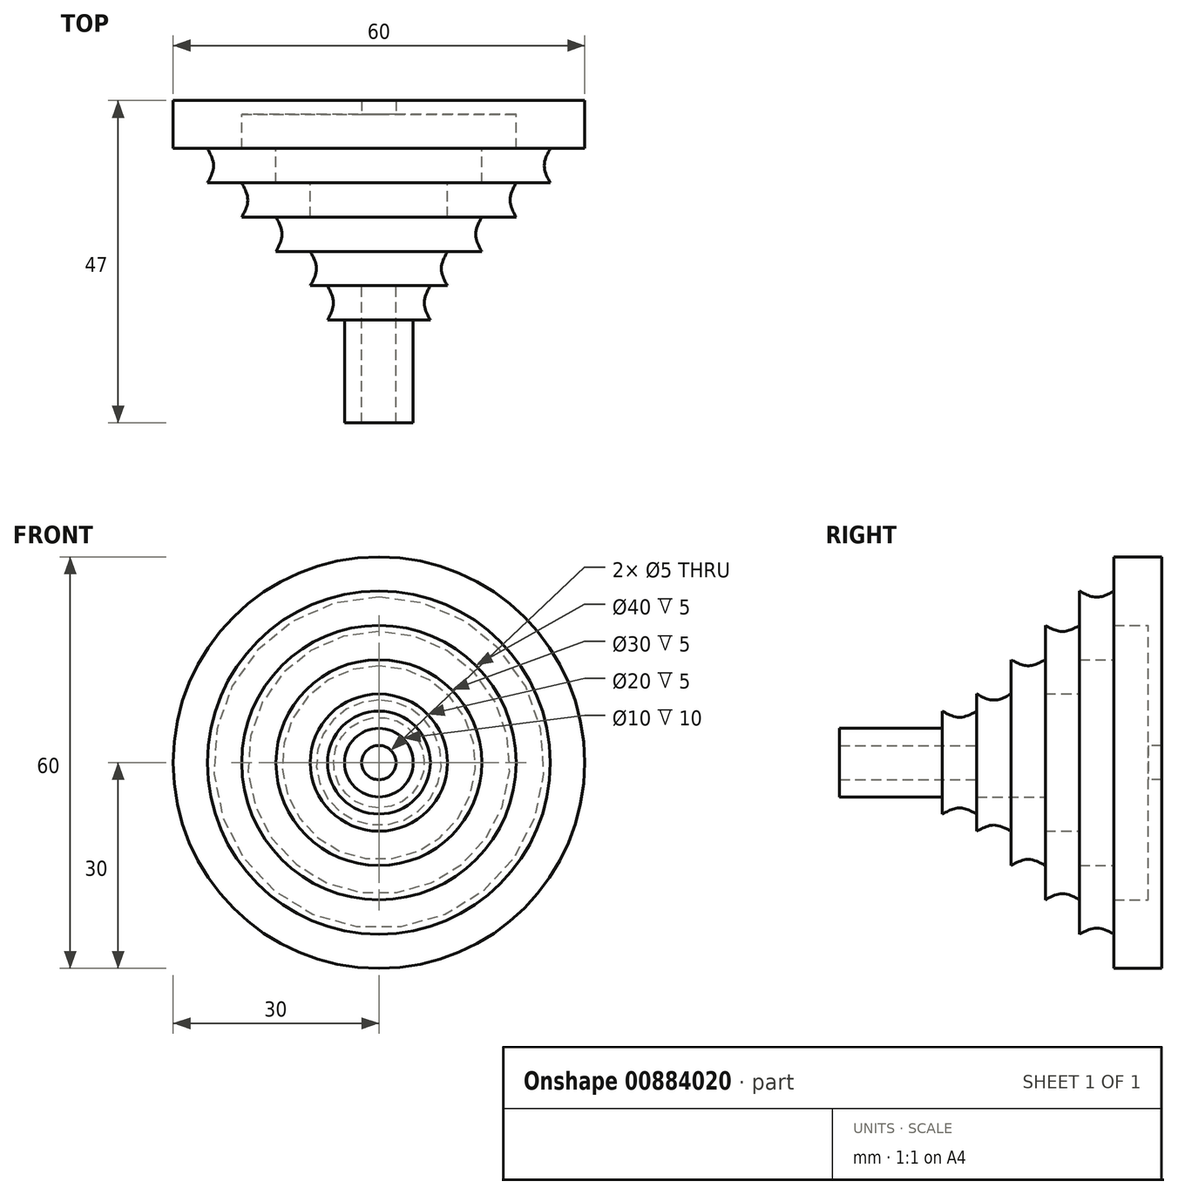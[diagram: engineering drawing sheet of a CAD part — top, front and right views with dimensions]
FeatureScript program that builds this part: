
annotation { "Feature Type Name" : "Feature", "Feature Type Description" : "" }
export const myFeature = defineFeature(function(context is Context, id is Id, definition is map)
    precondition{}
    {
        {
            var Q0;
            Q0=qCreatedBy(makeId("Front.planeOp"),FACE);
            var sketch = newSketch(context, id + "F0", { "sketchPlane" : qUnion([Q0])});
            skCircle(sketch, "E0", {"center": v(0, 0) * mm, "radius": 30 * mm});
            skCircle(sketch, "E1", {"center": v(0, 0) * mm, "radius": 20 * mm});
            skSolve(sketch);
        }
        {
            var Q0;
            Q0=makeQuery(id+"F0.imprint","IMPRINT",FACE,{"disambiguationData":[TD([[makeQuery(id+"F0.imprint","IMPRINT",EDGE,{"derivedFrom":sQuery(id+"F0.wireOp",EDGE,"E0")}),1.0]])]});
            extrude(context, id + "F1", {"entities" : qUnion([Q0]), "depth" : 5 * mm, "offsetDistance" : 25 * mm});
        }
        {
            var Q0;
            Q0=makeQuery(id+"F1.opExtrude","CAP_FACE",FACE,{"disambiguationData":[OSD([sQuery(id+"F0.wireOp",EDGE,"E0"),sQuery(id+"F0.wireOp",EDGE,"E1")])],"isStart":false});
            var sketch = newSketch(context, id + "F2", { "sketchPlane" : qUnion([Q0])});
            skCircle(sketch, "E2", {"center": v(0, 0) * mm, "radius": 25 * mm});
            skCircle(sketch, "E3", {"center": v(0, 0) * mm, "radius": 15 * mm});
            skSolve(sketch);
        }
        {
            var Q0;
            Q0=makeQuery(id+"F2.imprint","IMPRINT",FACE,{"disambiguationData":[TD([[makeQuery(id+"F2.imprint","IMPRINT",EDGE,{"derivedFrom":sQuery(id+"F2.wireOp",EDGE,"E3")}),-1.0]])]});
            var Q1;
            Q1=makeQuery(id+"F2.imprint","IMPRINT",FACE,{"disambiguationData":[TD([[makeQuery(id+"F2.imprint","IMPRINT",EDGE,{"derivedFrom":sQuery(id+"F2.wireOp",EDGE,"E2")}),1.0]])]});
            extrude(context, id + "F3", {"entities" : qUnion([Q0, Q1]), "operationType" : NewBodyOperationType.ADD, "depth" : 5 * mm, "offsetDistance" : 25 * mm});
        }
        {
            var Q0;
            Q0=makeQuery(id+"F3.opExtrude","CAP_FACE",FACE,{"disambiguationData":[OSD([sQuery(id+"F2.wireOp",EDGE,"E2"),sQuery(id+"F2.wireOp",EDGE,"E3")])],"isStart":false});
            var sketch = newSketch(context, id + "F4", { "sketchPlane" : qUnion([Q0])});
            skCircle(sketch, "E4", {"center": v(0, 0) * mm, "radius": 20 * mm});
            skCircle(sketch, "E5", {"center": v(0, 0) * mm, "radius": 10 * mm});
            skSolve(sketch);
        }
        {
            var Q0;
            Q0=makeQuery(id+"F4.imprint","IMPRINT",FACE,{"disambiguationData":[TD([[makeQuery(id+"F4.imprint","IMPRINT",EDGE,{"derivedFrom":sQuery(id+"F4.wireOp",EDGE,"E4")}),1.0]])]});
            var Q1;
            Q1=makeQuery(id+"F4.imprint","IMPRINT",FACE,{"disambiguationData":[TD([[makeQuery(id+"F4.imprint","IMPRINT",EDGE,{"derivedFrom":sQuery(id+"F4.wireOp",EDGE,"E5")}),-1.0]])]});
            extrude(context, id + "F5", {"entities" : qUnion([Q0, Q1]), "operationType" : NewBodyOperationType.ADD, "depth" : 5 * mm, "offsetDistance" : 25 * mm});
        }
        {
            var Q0;
            Q0=makeQuery(id+"F5.opExtrude","CAP_FACE",FACE,{"disambiguationData":[OSD([sQuery(id+"F4.wireOp",EDGE,"E4"),sQuery(id+"F4.wireOp",EDGE,"E5")])],"isStart":false});
            var sketch = newSketch(context, id + "F6", { "sketchPlane" : qUnion([Q0])});
            skCircle(sketch, "E6", {"center": v(0, 0) * mm, "radius": 15 * mm});
            skCircle(sketch, "E7", {"center": v(0, 0) * mm, "radius": 5 * mm});
            skSolve(sketch);
        }
        {
            var Q0;
            Q0=makeQuery(id+"F6.imprint","IMPRINT",FACE,{"disambiguationData":[TD([[makeQuery(id+"F6.imprint","IMPRINT",EDGE,{"derivedFrom":sQuery(id+"F6.wireOp",EDGE,"E7")}),-1.0]])]});
            var Q1;
            Q1=makeQuery(id+"F6.imprint","IMPRINT",FACE,{"disambiguationData":[TD([[makeQuery(id+"F6.imprint","IMPRINT",EDGE,{"derivedFrom":sQuery(id+"F6.wireOp",EDGE,"E6")}),1.0]])]});
            extrude(context, id + "F7", {"entities" : qUnion([Q0, Q1]), "operationType" : NewBodyOperationType.ADD, "depth" : 5 * mm, "offsetDistance" : 25 * mm});
        }
        {
            var Q0;
            Q0=makeQuery(id+"F7.opExtrude","CAP_FACE",FACE,{"disambiguationData":[OSD([sQuery(id+"F6.wireOp",EDGE,"E6"),sQuery(id+"F6.wireOp",EDGE,"E7")])],"isStart":false});
            var sketch = newSketch(context, id + "F8", { "sketchPlane" : qUnion([Q0])});
            skCircle(sketch, "E8", {"center": v(0, 0) * mm, "radius": 10 * mm});
            skSolve(sketch);
        }
        {
            var Q0;
            Q0=makeQuery(id+"F8.imprint","IMPRINT",FACE,{"disambiguationData":[TD([[makeQuery(id+"F8.imprint","IMPRINT",EDGE,{"derivedFrom":sQuery(id+"F8.wireOp",EDGE,"E8")}),1.0]])]});
            extrude(context, id + "F9", {"entities" : qUnion([Q0]), "operationType" : NewBodyOperationType.ADD, "depth" : 5 * mm, "offsetDistance" : 25 * mm});
        }
        {
            var Q0;
            Q0=qCreatedBy(makeId("Right.planeOp"),FACE);
            var sketch = newSketch(context, id + "F10", { "sketchPlane" : qUnion([Q0])});
            skFitSpline(sketch, "E9", {"points": [v(-5, 25) * mm, v(-7.5, 24.11) * mm, v(-10, 25) * mm], "startDerivative": vector(-5, -2.81) * mm, "endDerivative": vector(-4.95, 2.81) * mm});
            skLineSegment(sketch, "E10", {"start": v(-10, 25) * mm, "end": v(-5, 25) * mm});
            skFitSpline(sketch, "E11", {"points": [v(-10, 20) * mm, v(-12.5, 19.11) * mm, v(-15, 20) * mm], "startDerivative": vector(-5, -2.81) * mm, "endDerivative": vector(-4.95, 2.81) * mm});
            skLineSegment(sketch, "E12", {"start": v(-15, 20) * mm, "end": v(-10, 20) * mm});
            skFitSpline(sketch, "E13", {"points": [v(-15, 15) * mm, v(-17.5, 14.11) * mm, v(-20, 15) * mm], "startDerivative": vector(-5, -2.81) * mm, "endDerivative": vector(-4.95, 2.81) * mm});
            skLineSegment(sketch, "E14", {"start": v(-20, 15) * mm, "end": v(-15, 15) * mm});
            skFitSpline(sketch, "E15", {"points": [v(-20, 10) * mm, v(-22.5, 9.11) * mm, v(-25, 10) * mm], "startDerivative": vector(-5, -2.81) * mm, "endDerivative": vector(-4.95, 2.81) * mm});
            skLineSegment(sketch, "E16", {"start": v(-25, 10) * mm, "end": v(-20, 10) * mm});
            skSolve(sketch);
        }
        {
            var Q0;
            Q0=qCreatedBy(makeId("Right.planeOp"),FACE);
            var sketch = newSketch(context, id + "F11", { "sketchPlane" : qUnion([Q0])});
            skLineSegment(sketch, "E17", {"start": v(0, 0) * mm, "end": v(41.27, 0) * mm});
            skLineSegment(sketch, "E18", {"start": v(41.27, 0) * mm, "end": v(-57.31, 0) * mm});
            skSolve(sketch);
        }
        {
            var Q0;
            Q0 = qSketchRegion(id + "F10", true);
            var Q1;
            Q1=sQuery(id+"F11.wireOp",EDGE,"E17");
            revolve(context, id + "F12", {"operationType" : NewBodyOperationType.REMOVE, "surfaceOperationType" : NewSurfaceOperationType.NEW, "entities" : qUnion([Q0]), "axis" : qUnion([Q1]), "revolveType" : RevolveType.FULL, "oppositeDirection" : true});
        }
        {
            var Q0;
            Q0=makeQuery(id+"F9.opExtrude","CAP_FACE",FACE,{"disambiguationData":[OSD([sQuery(id+"F6.wireOp",EDGE,"E7"),sQuery(id+"F8.wireOp",EDGE,"E8")])],"isStart":false});
            var sketch = newSketch(context, id + "F13", { "sketchPlane" : qUnion([Q0])});
            skCircle(sketch, "E19", {"center": v(0, 0) * mm, "radius": 7.5 * mm});
            skCircle(sketch, "E20", {"center": v(0, 0) * mm, "radius": 2.5 * mm});
            skSolve(sketch);
        }
        {
            var Q0;
            Q0=makeQuery(id+"F13.imprint","IMPRINT",FACE,{"disambiguationData":[TD([[makeQuery(id+"F13.imprint","IMPRINT",EDGE,{"derivedFrom":sQuery(id+"F13.wireOp",EDGE,"E19")}),1.0]])]});
            var Q1;
            Q1=makeQuery(id+"F13.imprint","IMPRINT",FACE,{"disambiguationData":[TD([[makeQuery(id+"F13.imprint","IMPRINT",EDGE,{"derivedFrom":sQuery(id+"F13.wireOp",EDGE,"E20")}),-1.0]])]});
            extrude(context, id + "F14", {"entities" : qUnion([Q0, Q1]), "operationType" : NewBodyOperationType.ADD, "depth" : 5 * mm, "offsetDistance" : 25 * mm});
        }
        {
            var Q0;
            Q0=makeQuery(id+"F14.opExtrude","CAP_FACE",FACE,{"disambiguationData":[OSD([sQuery(id+"F13.wireOp",EDGE,"E19"),sQuery(id+"F13.wireOp",EDGE,"E20")])],"isStart":false});
            var sketch = newSketch(context, id + "F15", { "sketchPlane" : qUnion([Q0])});
            skCircle(sketch, "E21", {"center": v(0, 0) * mm, "radius": 5 * mm});
            skCircle(sketch, "E22", {"center": v(0, 0) * mm, "radius": 2.5 * mm});
            skSolve(sketch);
        }
        {
            var Q0;
            Q0=makeQuery(id+"F15.imprint","IMPRINT",FACE,{"disambiguationData":[TD([[makeQuery(id+"F15.imprint","IMPRINT",EDGE,{"derivedFrom":sQuery(id+"F15.wireOp",EDGE,"E21")}),1.0]])]});
            extrude(context, id + "F16", {"entities" : qUnion([Q0]), "operationType" : NewBodyOperationType.ADD, "depth" : 15 * mm, "offsetDistance" : 25 * mm});
        }
        {
            var Q0;
            Q0=qCreatedBy(makeId("Right.planeOp"),FACE);
            var sketch = newSketch(context, id + "F17", { "sketchPlane" : qUnion([Q0])});
            skFitSpline(sketch, "E23", {"points": [v(-25, 7.5) * mm, v(-27.5, 6.61) * mm, v(-30, 7.5) * mm], "startDerivative": vector(-5, -2.81) * mm, "endDerivative": vector(-4.95, 2.81) * mm});
            skLineSegment(sketch, "E24", {"start": v(-30, 7.5) * mm, "end": v(-25, 7.5) * mm});
            skLineSegment(sketch, "E25", {"start": v(0, 0) * mm, "end": v(-60.57, 0) * mm});
            skSolve(sketch);
        }
        {
            var Q0;
            Q0 = qSketchRegion(id + "F17", true);
            var Q1;
            Q1=sQuery(id+"F17.wireOp",EDGE,"E25");
            revolve(context, id + "F18", {"operationType" : NewBodyOperationType.REMOVE, "surfaceOperationType" : NewSurfaceOperationType.NEW, "entities" : qUnion([Q0]), "axis" : qUnion([Q1]), "revolveType" : RevolveType.FULL, "oppositeDirection" : true});
        }
        {
            var Q0;
            Q0=makeQuery(id+"F1.opExtrude","CAP_FACE",FACE,{"disambiguationData":[OSD([sQuery(id+"F0.wireOp",EDGE,"E0"),sQuery(id+"F0.wireOp",EDGE,"E1")])],"isStart":true});
            var sketch = newSketch(context, id + "F19", { "sketchPlane" : qUnion([Q0])});
            skCircle(sketch, "E26", {"center": v(0, 0) * mm, "radius": 30 * mm});
            skCircle(sketch, "E27", {"center": v(0, 0) * mm, "radius": 2.5 * mm});
            skSolve(sketch);
        }
        {
            var Q0;
            Q0 = qSketchRegion(id + "F19", true);
            extrude(context, id + "F20", {"entities" : qUnion([Q0]), "operationType" : NewBodyOperationType.ADD, "depth" : 2 * mm, "offsetDistance" : 25 * mm});
        }
    });
